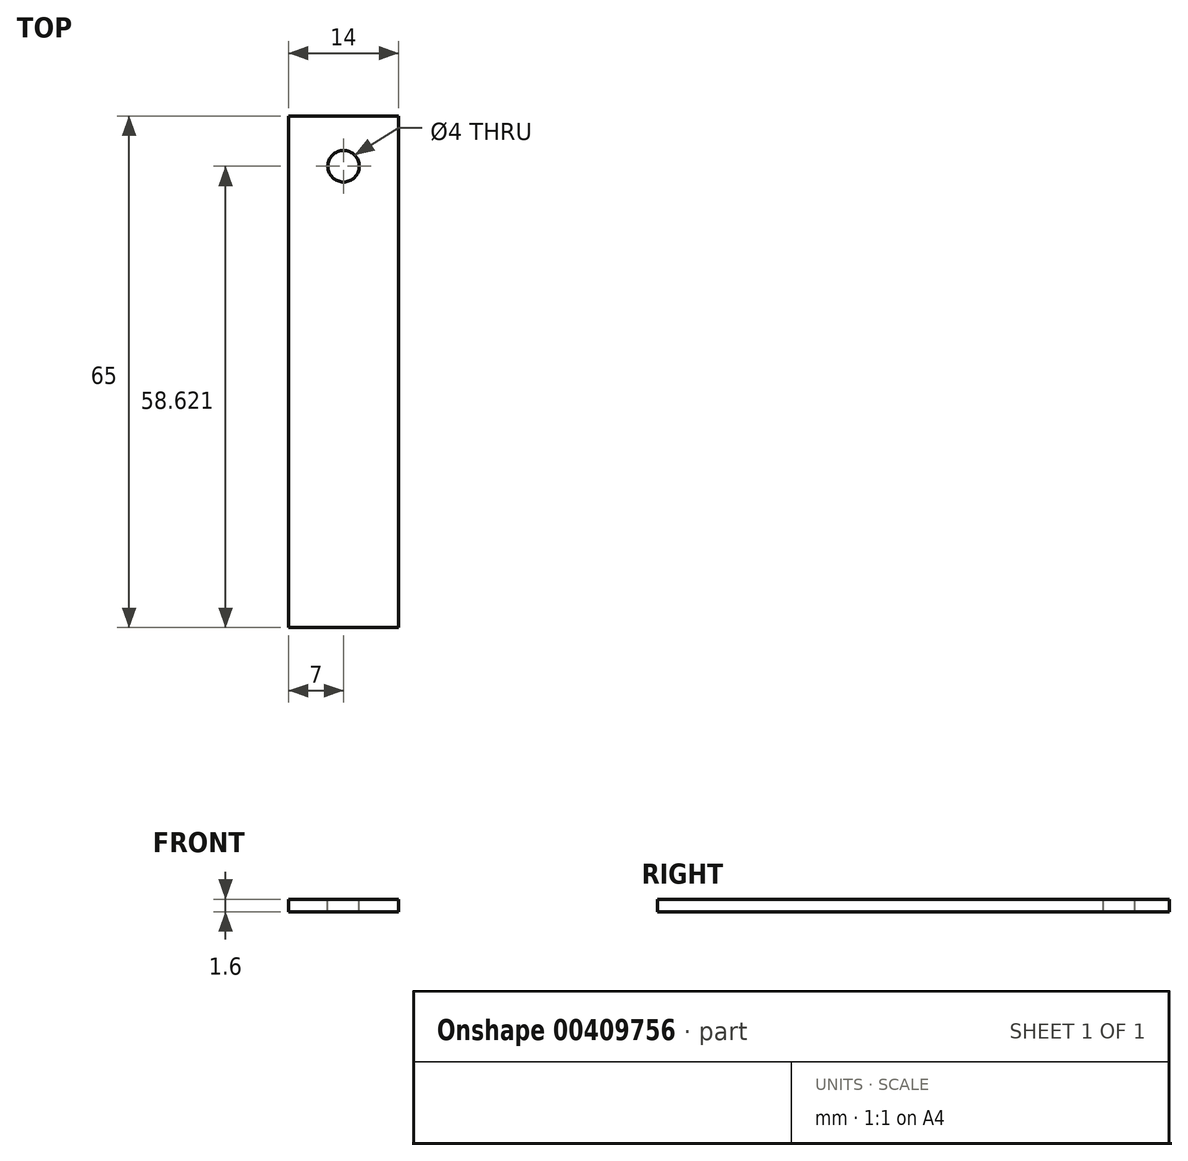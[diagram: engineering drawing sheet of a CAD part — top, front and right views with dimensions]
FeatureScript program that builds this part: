
annotation { "Feature Type Name" : "Feature", "Feature Type Description" : "" }
export const myFeature = defineFeature(function(context is Context, id is Id, definition is map)
    precondition{}
    {
        {
            var Q0;
            Q0=qCreatedBy(makeId("Top.planeOp"),FACE);
            var sketch = newSketch(context, id + "F0", { "sketchPlane" : qUnion([Q0])});
            skLineSegment(sketch, "E0.bottom", {"start": v(7, -32.5) * mm, "end": v(-7, -32.5) * mm});
            skLineSegment(sketch, "E0.top", {"start": v(7, 32.5) * mm, "end": v(-7, 32.5) * mm});
            skLineSegment(sketch, "E0.left", {"start": v(7, -32.5) * mm, "end": v(7, 32.5) * mm});
            skLineSegment(sketch, "E0.right", {"start": v(-7, -32.5) * mm, "end": v(-7, 32.5) * mm});
            skPoint(sketch, "E0.middle", {"position": v(0, 0) * mm});
            skCircle(sketch, "E1", {"center": v(0, 26.12) * mm, "radius": 2 * mm});
            skSolve(sketch);
        }
        {
            var Q0;
            Q0=makeQuery(id+"F0.imprint","IMPRINT",FACE,{"disambiguationData":[TD([[makeQuery(id+"F0.imprint","IMPRINT",EDGE,{"derivedFrom":sQuery(id+"F0.wireOp",EDGE,"E0.bottom")}),-1.0]])]});
            extrude(context, id + "F1", {"entities" : qUnion([Q0]), "oppositeDirection" : true, "depth" : 1.6 * mm});
        }
    });
